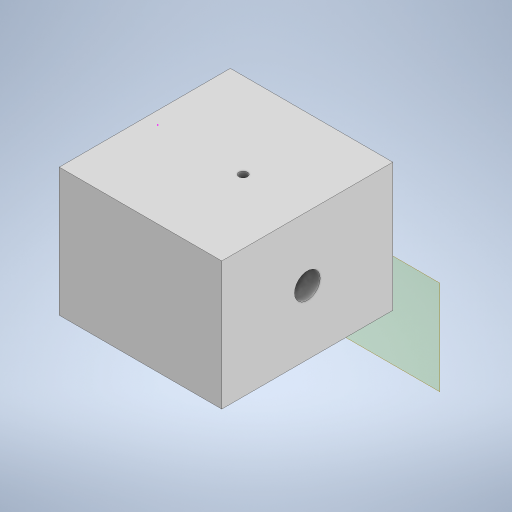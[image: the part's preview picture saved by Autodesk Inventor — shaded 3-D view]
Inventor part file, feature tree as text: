
AUTODESK INVENTOR PART (.ipt)
format: ipt  version: 2023 (Build 270158000, 158)  size: 289,280 bytes
history: native  units: mm
features: sketch x9, extrude x7, plane x6
ambient origin geometry x8: Origin, YZ Plane, XZ Plane, XY Plane, X Axis, Y Axis, Z Axis, Center Point
bodies: Body1 (feature_tree)
feature tree (22):
  plane  "Work Plane13"
  extrude  "Extrusion34"  Depth=40.0mm
  sketch  "Sketch46"  dims[d144=30.0mm d145=0.0mm d146=36.0mm]
  plane  "Work Plane11"
  extrude  "Extrusion35"  Depth=36.0mm
  sketch  "Sketch48"  dims[d150=0.0mm d151=0.0mm d156=20.0mm]
  extrude  "Extrusion36"  Depth=2.0mm
  plane  "Work Plane7"
  extrude  "Extrusion38"  Depth=20.0mm
  plane  "Work Plane4"
  extrude  "Extrusion39"  Depth=15.0mm TaperAngle=0.0deg
  plane  "Work Plane1"
  plane  "Work Plane6"
  extrude  "Extrusion42"  Depth=20.0mm
  extrude  "Extrusion44"  Depth=6.0mm
  sketch  "Sketch45"  dims[d142=38.0mm d143=40.0mm]
  sketch  "Sketch47"  dims[d147=30.0mm d148=-2.617994mm d149=2.0mm]
  sketch  "Sketch49"  dims[d157=15.0mm d158=15.0mm d159=0.0mm]
  sketch  "Sketch58"  dims[d160=3.2mm d161=20.0mm]
  sketch  "Sketch59"  dims[d162=35.0mm d163=0.0mm d172=6.0mm]
  sketch  "Sketch62"  dims[d173=0.0mm d174=0.0mm]
  sketch  "Sketch65"  dims[d177=5.0mm d178=0.0mm d49=0.5mm d50=0.872665mm d51=0.5mm d52=0.872665mm d130=0.5mm d131=0.872665mm d132=0.5mm d133=0.872665mm]
